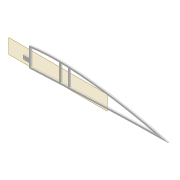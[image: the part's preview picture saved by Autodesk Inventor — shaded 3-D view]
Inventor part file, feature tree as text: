
AUTODESK INVENTOR PART (.ipt)
format: ipt  version: 2022 (Build 260153000, 153)  size: 414,720 bytes
history: native  units: mm
features: extrude x8, sketch x7, projected_geometry x6, fillet x2, shell x1, plane x1
ambient origin geometry x8: Origin, YZ Plane, XZ Plane, XY Plane, X Axis, Y Axis, Z Axis, Center Point
bodies: Solid1 (feature_tree)
feature tree (25):
  extrude  "Extrusion1"  Depth=5.0mm
  shell  "Shell1"  Thickness=2.0mm
  extrude  "Extrusion8"  Depth=5.9mm
  extrude  "Extrusion3"  Depth=10.0mm TaperAngle=0.0deg
  extrude  "Extrusion4"  Depth=2.0mm
  fillet  "Fillet1"  Radius=5.0mm
  sketch  "Sketch10"  dims[d22=4.0mm d23=0.0mm d31=2.0mm d32=5.0mm]
  extrude  "Extrusion5"  Depth=2.5mm
  plane  "Work Plane2"
  extrude  "Extrusion9"  Depth=1.6mm
  fillet  "Fillet2"  Radius=2.5mm
  extrude  "Extrusion10"  Depth=0.5mm
  extrude  "Extrusion11"  Depth=0.5mm TaperAngle=0.0deg
  sketch  "Sketch3"  dims[d0=4.0mm d1=0.0mm d2=5.0mm d7=2.0mm]
  sketch  "Sketch8"  dims[d8=2.0mm d9=5.9mm]
  sketch  "Sketch9"  dims[d13=10.0mm d14=0.0mm d16=10.0mm d17=0.0mm]
  projected_geometry  "Projected Loop4"
  projected_geometry  "Projected Loop10"
  sketch  "Sketch24"  dims[d34=1.6mm d35=2.5mm]
  projected_geometry  "Projected Loop11"
  projected_geometry  "Projected Loop12"
  projected_geometry  "Projected Loop13"
  sketch  "Sketch26"  dims[d37=5.0mm d38=1.6mm d40=2.5mm]
  projected_geometry  "Projected Loop14"
  sketch  "Sketch27"  dims[d62=80.0mm d63=6.0mm d64=4.0mm d65=0.0mm d66=3.0mm d67=12.0mm d68=5.0mm d69=17.0mm d70=12.0mm d71=3.05mm d72=10.0mm d73=0.0mm d74=2.0mm d75=100.0mm d77=20.0mm d78=0.5mm d79=10.0mm d80=0.0mm d81=10.0mm d82=0.0mm]
